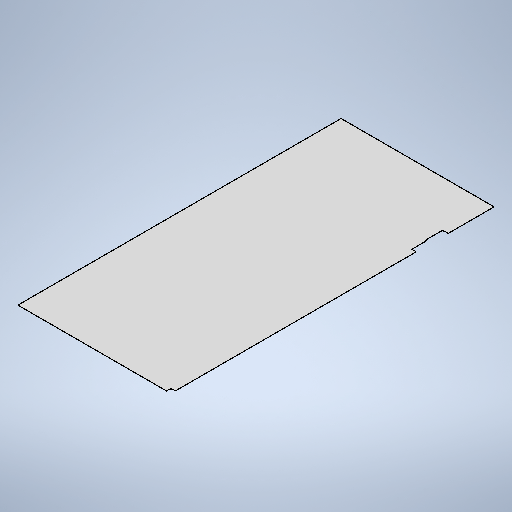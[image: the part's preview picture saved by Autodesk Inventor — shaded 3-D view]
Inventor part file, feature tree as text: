
AUTODESK INVENTOR PART (.ipt)
format: ipt  version: 2025.1 (Build 291241020, 241B)  size: 312,320 bytes
history: native  units: mm
features: other x2, sheet_metal_op x1, chamfer x1, sketch x1
ambient origin geometry x8: Origin, YZ Plane, XZ Plane, XY Plane, X Axis, Y Axis, Z Axis, Center Point
bodies: Body1 (feature_tree)
feature tree (5):
  sheet_metal_op  "Face3"
  chamfer  "Corner Round1"
  sketch  "Sketch1"  dims[d61=500.0mm d154=1385.0mm d155=2925.0mm d156=2.0mm d157=40.0mm d158=15.0mm d159=290.0mm d161=40.0mm d162=2220.0mm d163=10.0mm d164=150.0mm d165=5.0mm]
  other  "Plate5"
  other  "Definition1"
